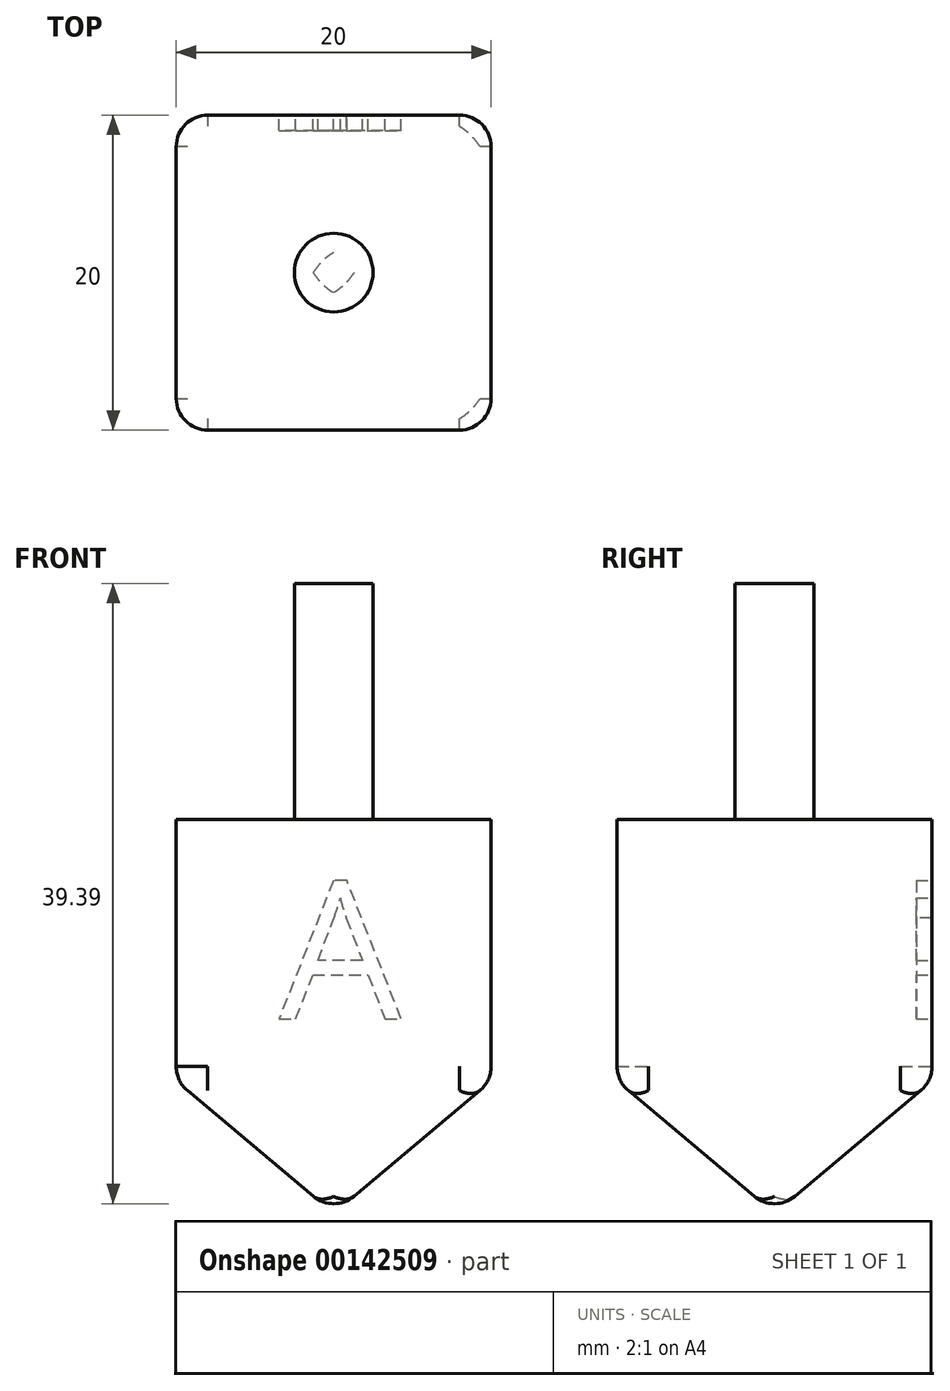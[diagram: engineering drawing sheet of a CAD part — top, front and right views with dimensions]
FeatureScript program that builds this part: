
annotation { "Feature Type Name" : "Feature", "Feature Type Description" : "" }
export const myFeature = defineFeature(function(context is Context, id is Id, definition is map)
    precondition{}
    {
        {
            var Q0;
            Q0=qCreatedBy(makeId("Top.planeOp"),FACE);
            var sketch = newSketch(context, id + "F0", { "sketchPlane" : qUnion([Q0])});
            skLineSegment(sketch, "E0.bottom", {"start": v(-10, 10) * mm, "end": v(10, 10) * mm});
            skLineSegment(sketch, "E0.top", {"start": v(-10, -10) * mm, "end": v(10, -10) * mm});
            skLineSegment(sketch, "E0.left", {"start": v(-10, 10) * mm, "end": v(-10, -10) * mm});
            skLineSegment(sketch, "E0.right", {"start": v(10, 10) * mm, "end": v(10, -10) * mm});
            skSolve(sketch);
        }
        {
            var Q0;
            Q0=makeQuery(id+"F0.imprint","IMPRINT",FACE,{"disambiguationData":[TD([[makeQuery(id+"F0.imprint","IMPRINT",EDGE,{"derivedFrom":sQuery(id+"F0.wireOp",EDGE,"E0.bottom")}),-1.0]])]});
            extrude(context, id + "F1", {"entities" : qUnion([Q0]), "oppositeDirection" : true, "depth" : 25 * mm});
        }
        {
            var Q0;
            Q0=makeQuery(id+"F1.opExtrude","CAP_FACE",FACE,{"disambiguationData":[OSD([sQuery(id+"F0.wireOp",EDGE,"E0.bottom"),sQuery(id+"F0.wireOp",EDGE,"E0.top"),sQuery(id+"F0.wireOp",EDGE,"E0.left"),sQuery(id+"F0.wireOp",EDGE,"E0.right")])],"isStart":true});
            var sketch = newSketch(context, id + "F2", { "sketchPlane" : qUnion([Q0])});
            skCircle(sketch, "E1", {"center": v(0, 0) * mm, "radius": 2.5 * mm});
            skSolve(sketch);
        }
        {
            var Q0;
            Q0 = qSketchRegion(id + "F2", true);
            extrude(context, id + "F3", {"entities" : qUnion([Q0]), "operationType" : NewBodyOperationType.ADD, "depth" : 15 * mm});
        }
        {
            var Q0;
            Q0=makeQuery(id+"F1.opExtrude","CAP_EDGE",EDGE,{"disambiguationData":[OSD([sQuery(id+"F0.wireOp",EDGE,"E0.bottom")])],"isStart":false});
            var Q1;
            Q1=makeQuery(id+"F1.opExtrude","CAP_EDGE",EDGE,{"disambiguationData":[OSD([sQuery(id+"F0.wireOp",EDGE,"E0.right")])],"isStart":false});
            var Q2;
            Q2=makeQuery(id+"F1.opExtrude","CAP_EDGE",EDGE,{"disambiguationData":[OSD([sQuery(id+"F0.wireOp",EDGE,"E0.top")])],"isStart":false});
            var Q3;
            Q3=makeQuery(id+"F1.opExtrude","CAP_EDGE",EDGE,{"disambiguationData":[OSD([sQuery(id+"F0.wireOp",EDGE,"E0.left")])],"isStart":false});
            chamfer(context, id + "F4", {"entities" : qUnion([Q0, Q1, Q2, Q3]), "chamferType" : ChamferType.OFFSET_ANGLE, "width" : 10 * mm, "oppositeDirection" : false, "angle" : 40 * degree, "tangentPropagation" : true});
        }
        {
            var Q0;
            Q0=makeQuery(id+"F1.opExtrude","SWEPT_EDGE",EDGE,{"disambiguationData":[OSD([sQuery(id+"F0.wireOp",EDGE,"E0.top"),sQuery(id+"F0.wireOp",EDGE,"E0.left")])]});
            var Q1;
            Q1=makeQuery(id+"F1.opExtrude","SWEPT_EDGE",EDGE,{"disambiguationData":[OSD([sQuery(id+"F0.wireOp",EDGE,"E0.top"),sQuery(id+"F0.wireOp",EDGE,"E0.right")])]});
            var Q2;
            Q2=makeQuery(id+"F1.opExtrude","SWEPT_EDGE",EDGE,{"disambiguationData":[OSD([sQuery(id+"F0.wireOp",EDGE,"E0.bottom"),sQuery(id+"F0.wireOp",EDGE,"E0.left")])]});
            var Q3;
            Q3=makeQuery(id+"F1.opExtrude","SWEPT_EDGE",EDGE,{"disambiguationData":[OSD([sQuery(id+"F0.wireOp",EDGE,"E0.bottom"),sQuery(id+"F0.wireOp",EDGE,"E0.right")])]});
            var Q4;
            Q4=makeQuery(id+"F4.opChamfer","BLEND_EDGE",EDGE,{"blendedFrom":[makeQuery(id+"F1.opExtrude","CAP_EDGE",EDGE,{"disambiguationData":[OSD([sQuery(id+"F0.wireOp",EDGE,"E0.top")])],"isStart":false}),makeQuery(id+"F1.opExtrude","CAP_EDGE",EDGE,{"disambiguationData":[OSD([sQuery(id+"F0.wireOp",EDGE,"E0.right")])],"isStart":false})],"blendedInto":[]});
            var Q5;
            Q5=makeQuery(id+"F4.opChamfer","BLEND_EDGE",EDGE,{"blendedFrom":[makeQuery(id+"F1.opExtrude","CAP_EDGE",EDGE,{"disambiguationData":[OSD([sQuery(id+"F0.wireOp",EDGE,"E0.bottom")])],"isStart":false}),makeQuery(id+"F1.opExtrude","CAP_EDGE",EDGE,{"disambiguationData":[OSD([sQuery(id+"F0.wireOp",EDGE,"E0.right")])],"isStart":false})],"blendedInto":[]});
            var Q6;
            Q6=makeQuery(id+"F4.opChamfer","BLEND_EDGE",EDGE,{"blendedFrom":[makeQuery(id+"F1.opExtrude","CAP_EDGE",EDGE,{"disambiguationData":[OSD([sQuery(id+"F0.wireOp",EDGE,"E0.bottom")])],"isStart":false}),makeQuery(id+"F1.opExtrude","CAP_EDGE",EDGE,{"disambiguationData":[OSD([sQuery(id+"F0.wireOp",EDGE,"E0.left")])],"isStart":false})],"blendedInto":[]});
            var Q7;
            Q7=makeQuery(id+"F4.opChamfer","BLEND_EDGE",EDGE,{"blendedFrom":[makeQuery(id+"F1.opExtrude","CAP_EDGE",EDGE,{"disambiguationData":[OSD([sQuery(id+"F0.wireOp",EDGE,"E0.top")])],"isStart":false}),makeQuery(id+"F1.opExtrude","CAP_EDGE",EDGE,{"disambiguationData":[OSD([sQuery(id+"F0.wireOp",EDGE,"E0.left")])],"isStart":false})],"blendedInto":[]});
            var Q8;
            {var subQ0=sQuery(id+"F0.wireOp",EDGE,"E0.top");Q8=makeQuery(id+"F4.opChamfer","BLEND_EDGE",EDGE,{"blendedFrom":[makeQuery(id+"F1.opExtrude","CAP_EDGE",EDGE,{"disambiguationData":[OSD([subQ0])],"isStart":false}),makeQuery(id+"F1.opExtrude","SWEPT_FACE",FACE,{"disambiguationData":[OSD([subQ0])]})],"blendedInto":[makeQuery(id+"F1.opExtrude","SWEPT_FACE",FACE,{"disambiguationData":[OSD([subQ0])]})]});}
            var Q9;
            {var subQ0=sQuery(id+"F0.wireOp",EDGE,"E0.left");Q9=makeQuery(id+"F4.opChamfer","BLEND_EDGE",EDGE,{"blendedFrom":[makeQuery(id+"F1.opExtrude","CAP_EDGE",EDGE,{"disambiguationData":[OSD([subQ0])],"isStart":false}),makeQuery(id+"F1.opExtrude","SWEPT_FACE",FACE,{"disambiguationData":[OSD([subQ0])]})],"blendedInto":[makeQuery(id+"F1.opExtrude","SWEPT_FACE",FACE,{"disambiguationData":[OSD([subQ0])]})]});}
            var Q10;
            {var subQ0=sQuery(id+"F0.wireOp",EDGE,"E0.right");Q10=makeQuery(id+"F4.opChamfer","BLEND_EDGE",EDGE,{"blendedFrom":[makeQuery(id+"F1.opExtrude","CAP_EDGE",EDGE,{"disambiguationData":[OSD([subQ0])],"isStart":false}),makeQuery(id+"F1.opExtrude","SWEPT_FACE",FACE,{"disambiguationData":[OSD([subQ0])]})],"blendedInto":[makeQuery(id+"F1.opExtrude","SWEPT_FACE",FACE,{"disambiguationData":[OSD([subQ0])]})]});}
            var Q11;
            {var subQ0=sQuery(id+"F0.wireOp",EDGE,"E0.bottom");Q11=makeQuery(id+"F4.opChamfer","BLEND_EDGE",EDGE,{"blendedFrom":[makeQuery(id+"F1.opExtrude","CAP_EDGE",EDGE,{"disambiguationData":[OSD([subQ0])],"isStart":false}),makeQuery(id+"F1.opExtrude","SWEPT_FACE",FACE,{"disambiguationData":[OSD([subQ0])]})],"blendedInto":[makeQuery(id+"F1.opExtrude","SWEPT_FACE",FACE,{"disambiguationData":[OSD([subQ0])]})]});}
            fillet(context, id + "F5", {"entities" : qUnion([Q0, Q1, Q2, Q3, Q4, Q5, Q6, Q7, Q8, Q9, Q10, Q11]), "radius" : 2 * mm, "tangentPropagation" : true, "allowEdgeOverflow" : false});
        }
        {
            var Q0;
            Q0=makeQuery(id+"F1.opExtrude","SWEPT_FACE",FACE,{"disambiguationData":[OSD([sQuery(id+"F0.wireOp",EDGE,"E0.bottom")])]});
            var sketch = newSketch(context, id + "F6", { "sketchPlane" : qUnion([Q0])});
            skText(sketch, "E2", { "text": "A", "fontName": "OpenSans-Regular.ttf"});
            const initialGuessF6  = {"E2": [-0.00429, -0.01265, 1, 0, 0.00882]};
            skSetInitialGuess(sketch, initialGuessF6);
            skSolve(sketch);
        }
        {
            var Q0;
            Q0 = qSketchRegion(id + "F6", true);
            extrude(context, id + "F7", {"entities" : qUnion([Q0]), "operationType" : NewBodyOperationType.REMOVE, "oppositeDirection" : true, "depth" : 1 * mm});
        }
    });
